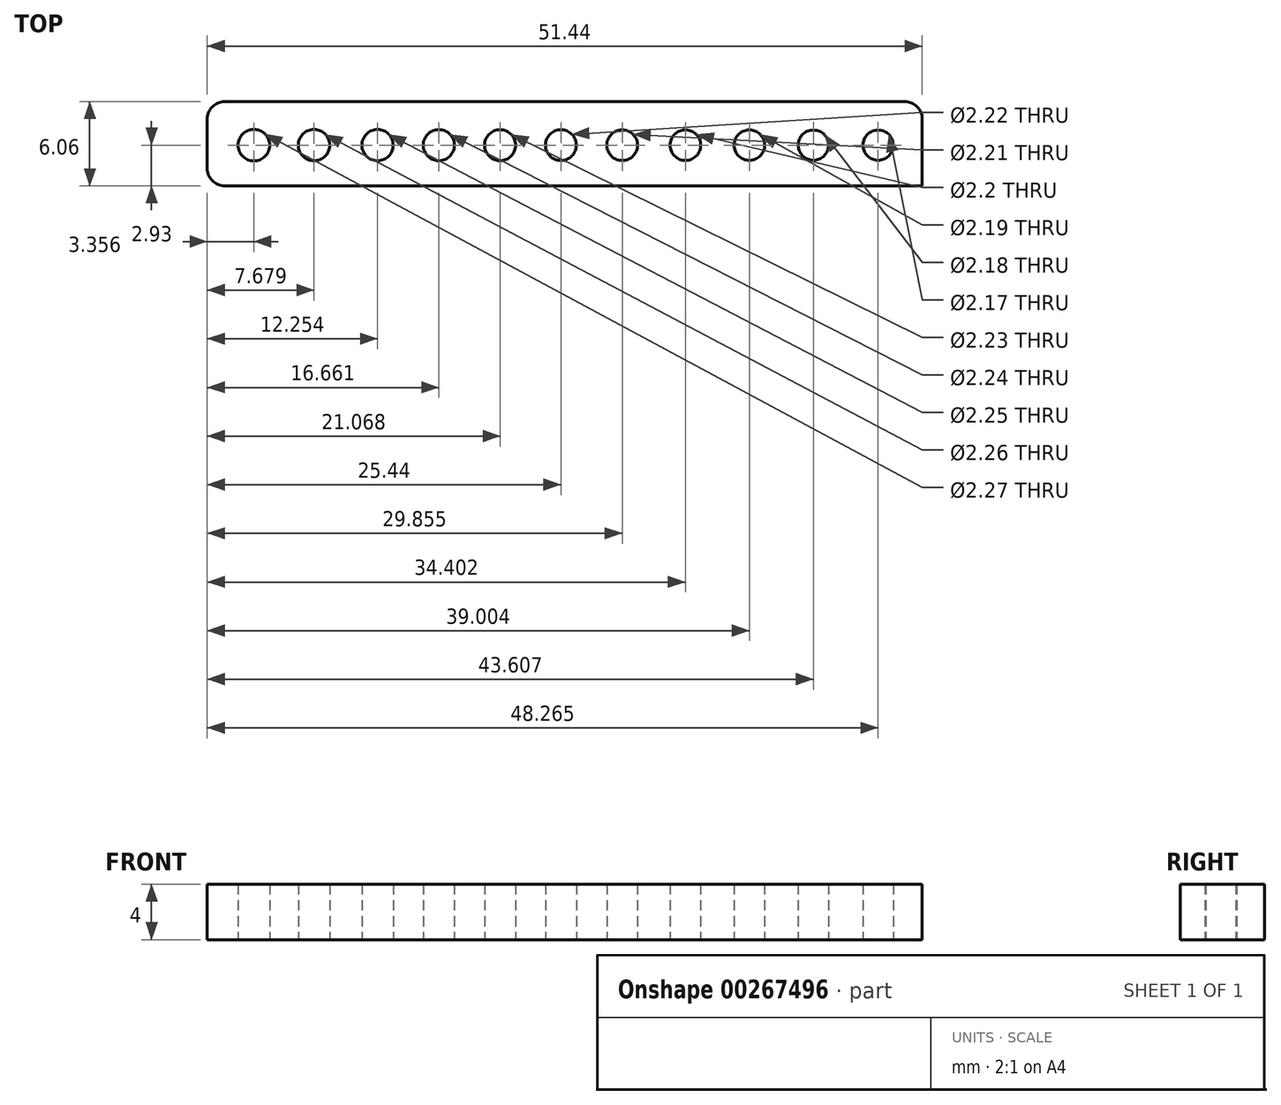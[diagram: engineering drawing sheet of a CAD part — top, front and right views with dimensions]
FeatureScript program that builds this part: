
annotation { "Feature Type Name" : "Feature", "Feature Type Description" : "" }
export const myFeature = defineFeature(function(context is Context, id is Id, definition is map)
    precondition{}
    {
        {
            var Q0;
            Q0=qCreatedBy(makeId("Top.planeOp"),FACE);
            var sketch = newSketch(context, id + "F0", { "sketchPlane" : qUnion([Q0])});
            skCircle(sketch, "E0", {"center": v(0, 0) * mm, "radius": 1.11 * mm});
            skCircle(sketch, "E1", {"center": v(4.41, 0) * mm, "radius": 1.1 * mm});
            skCircle(sketch, "E2", {"center": v(8.96, 0) * mm, "radius": 1.1 * mm});
            skCircle(sketch, "E3", {"center": v(13.56, 0) * mm, "radius": 1.1 * mm});
            skCircle(sketch, "E4", {"center": v(18.17, 0) * mm, "radius": 1.09 * mm});
            skCircle(sketch, "E5", {"center": v(22.82, 0) * mm, "radius": 1.08 * mm});
            skCircle(sketch, "E6", {"center": v(-4.37, 0) * mm, "radius": 1.12 * mm});
            skCircle(sketch, "E7", {"center": v(-8.78, 0) * mm, "radius": 1.12 * mm});
            skCircle(sketch, "E8", {"center": v(-13.19, 0) * mm, "radius": 1.13 * mm});
            skCircle(sketch, "E9", {"center": v(-17.76, 0) * mm, "radius": 1.13 * mm});
            skCircle(sketch, "E10", {"center": v(-22.08, 0) * mm, "radius": 1.14 * mm});
            skLineSegment(sketch, "E11.bottom", {"start": v(-24.17, 3.13) * mm, "end": v(24.73, 3.13) * mm});
            skLineSegment(sketch, "E11.top", {"start": v(-24.17, -2.93) * mm, "end": v(26, -2.93) * mm});
            skLineSegment(sketch, "E11.left", {"start": v(-25.44, 1.86) * mm, "end": v(-25.44, -1.66) * mm});
            skLineSegment(sketch, "E11.right", {"start": v(26, 1.86) * mm, "end": v(26, -2.93) * mm});
            skPoint(sketch, "E12.visualSharp", {"position": v(-25.44, 3.13) * mm});
            skArc(sketch, "E12.filletArc", {"start": v(-24.17, 3.13) * mm, "mid": v(-25.07, 2.76) * mm, "end": v(-25.44, 1.86) * mm});
            skPoint(sketch, "E13.visualSharp", {"position": v(-25.44, -2.93) * mm});
            skArc(sketch, "E13.filletArc", {"start": v(-25.44, -1.66) * mm, "mid": v(-25.07, -2.56) * mm, "end": v(-24.17, -2.93) * mm});
            skPoint(sketch, "E14.visualSharp", {"position": v(26, 3.13) * mm});
            skArc(sketch, "E14.filletArc", {"start": v(26, 1.86) * mm, "mid": v(25.63, 2.76) * mm, "end": v(24.73, 3.13) * mm});
            skSolve(sketch);
        }
        {
            var Q0;
            Q0=makeQuery(id+"F0.imprint","IMPRINT",FACE,{"disambiguationData":[TD([[makeQuery(id+"F0.imprint","IMPRINT",EDGE,{"derivedFrom":sQuery(id+"F0.wireOp",EDGE,"E0")}),-1.0]])]});
            extrude(context, id + "F1", {"entities" : qUnion([Q0]), "depth" : 4 * mm});
        }
    });
